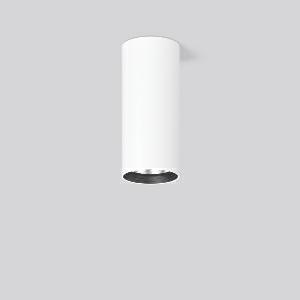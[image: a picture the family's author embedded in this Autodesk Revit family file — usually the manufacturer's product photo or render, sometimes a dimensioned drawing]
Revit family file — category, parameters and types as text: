
# Revit family: heledon_mini_a_931201_002_3_76_4706
name_source: partatom
category: Lighting Fixtures
units: mm (PartAtom-declared; Revit-internal decimal feet)

## family parameters
Cut with Voids When Loaded = No
Host = Face
Light Source = No
Part Type = Normal
Room Calculation Point = No
Round Connector Dimension = Use Diameter
Shared = No

## types (1)
- HELEDON mini A (1 x LED Modul 935, 2500 lm, 3500)
    Apparent Load = 20 VA
    Approval mark = CE
    CIE Flux Codes = 99 100 100 100 100
    Color Rendering = 92
    Color Temperature = 3500
    Default Elevation = 1800 mm
    Description = Series: HELEDON mini
Cylindrical surface-mounted downlight. Housing: die-cast aluminium, powder-coated. Internal ceiling frame polycarbonate with bayonet mounting. Black plastic ring and recessed LED to prevent glare from the side. Optical assembly with reflector made of MIRO-Silver with 98% total light reflection for outstanding efficiency - can be changed without tools. Best colour rendering index Ra>90. Suitable for Ceiling mounting. Easy installation with a separate ceiling frame with bayonet mounting and plug connection. Driver integrated. Connected via plug-in connector. High quality converter without flickering and stroboscopic effect. The following accessories can be mounted without use of tools: interchangeable lenses, decorative glasses, honeycomb louvre, clear and frosted diffusers, white interchangeable plastic ring. 
Colour: traffic white, matt (RAL 9016)
Diameter: 87 mm
Height: 197 mm
Lamp: LED
Socket: without socket
Colour temperature: 3500K
Colour rendering index (CRI): 92
System power: 20 W
Rated luminous flux: 2500 lm
Luminous efficiency: 125 lm/W
Control gear: Converter, dimmable, DALI
Protection class: I
Type of protection: IP 20
    Height = 197 mm
    Lamp = 1 x LED Modul 935
    Lamp Light Flux = 2500 lm
    Lamp count = 1
    Length = 87 mm
    Lifetime = 50000 h
    Luminous efficacy = 125 lm/W
    Manufacturer = RZB
    ModVariant = No
    Model = 931201.002.3.76
    Mounting Place = Ceiling
    Mounting Type = Surface mounted
    Number of Poles = 1
    OnlyDefault = Yes
    Power Factor = 1
    Product Name = HELEDON mini A
    Product group = Surface mounted downlights
    ProductGroupID = 302
    Protection Class = Protection class I
    Protection Degree = IP 20
    RLX_Detail_Level = 1
    RLX_Emergency_Light_Flux = 0 lm
    RLX_Emergency_Type = 0
    RLX_Emergency_Type_DB = No
    RlxData = <blob elided: 104729 chars, md5=cc6ceec1>
    Socket = socket
    Standby Power = 0 W
    System Light Flux = 2500 lm
    System Power = 20 W
    Type Comments = Product without accessories
    Type Image = 931188.002.jpg
    URL = http://relux.com
    VarID = ---
    Voltage = 230 V
    Voltage Range = 220-240 V
    Weight = 0.00 kg
    Width = 0 mm  [stored 0 ft]

note: [stored X ft] marks values corroborated as IEEE doubles in the binary element streams (Revit-internal decimal feet)

## geometry (parser evidence)
native form markers: Blend x4, Sweep x9
no freeform markers — native parametric forms only
